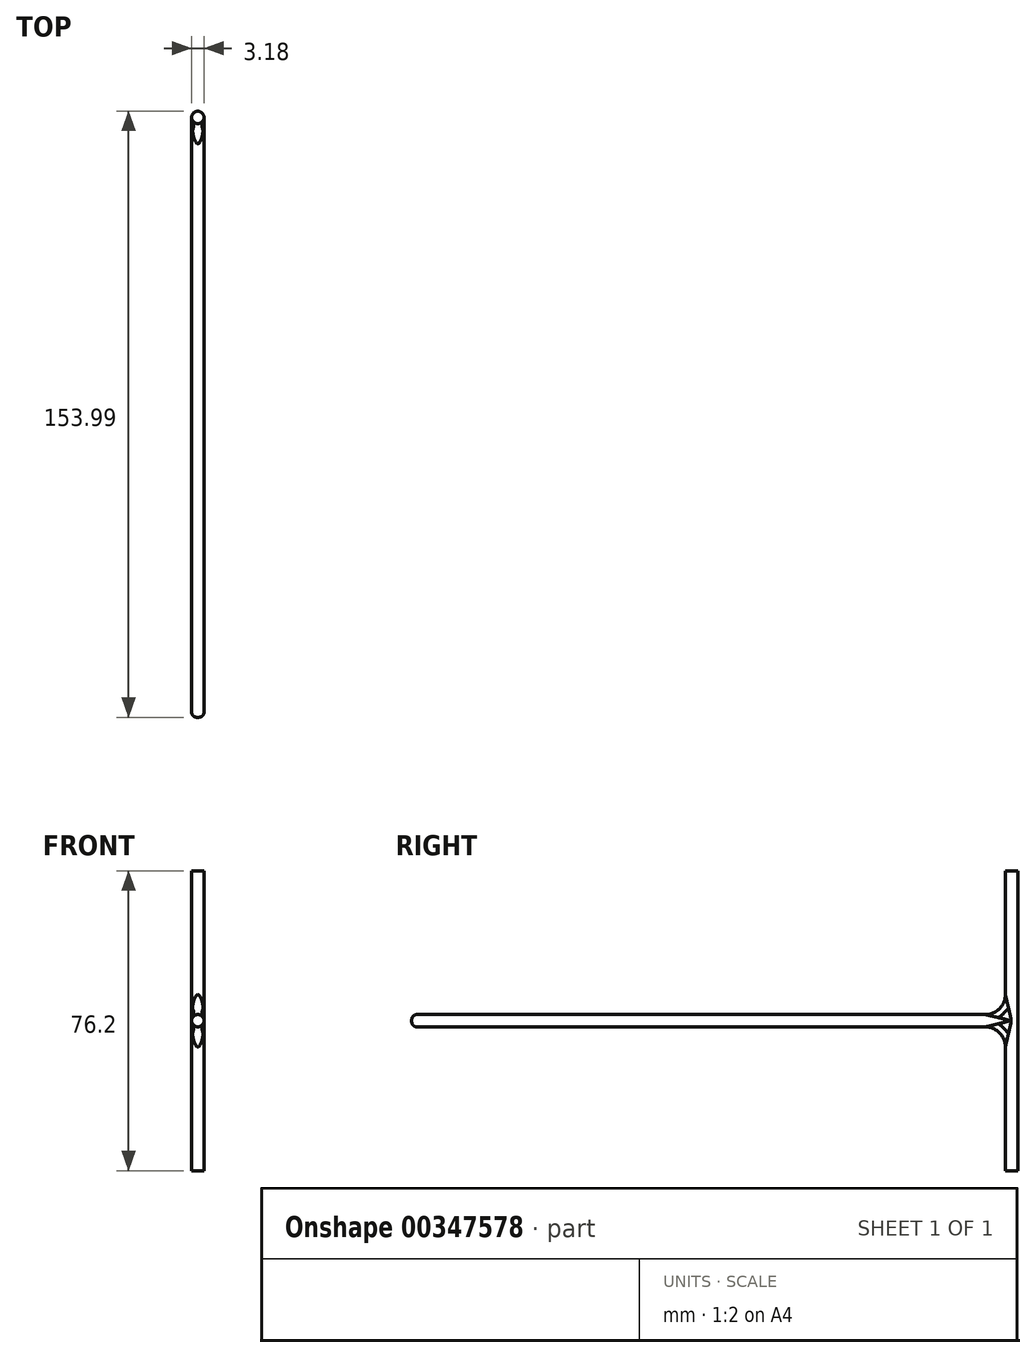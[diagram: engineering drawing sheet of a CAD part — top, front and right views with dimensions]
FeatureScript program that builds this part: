
annotation { "Feature Type Name" : "Feature", "Feature Type Description" : "" }
export const myFeature = defineFeature(function(context is Context, id is Id, definition is map)
    precondition{}
    {
        {
            var Q0;
            Q0=qCreatedBy(makeId("Front.planeOp"),FACE);
            var sketch = newSketch(context, id + "F0", { "sketchPlane" : qUnion([Q0])});
            skCircle(sketch, "E0", {"center": v(0, 0) * mm, "radius": 1.56 * mm});
            skSolve(sketch);
        }
        {
            var Q0;
            Q0 = qSketchRegion(id + "F0", true);
            extrude(context, id + "F1", {"entities" : qUnion([Q0]), "depth" : 152.4 * mm});
        }
        {
            var Q0;
            Q0=makeQuery(id+"F1.opExtrude","CAP_EDGE",EDGE,{"disambiguationData":[OSD([sQuery(id+"F0.wireOp",EDGE,"E0")])],"isStart":false});
            fillet(context, id + "F2", {"entities" : qUnion([Q0]), "radius" : 1.27 * mm, "tangentPropagation" : true, "allowEdgeOverflow" : false});
        }
        {
            var Q0;
            Q0=qCreatedBy(makeId("Top.planeOp"),FACE);
            var sketch = newSketch(context, id + "F3", { "sketchPlane" : qUnion([Q0])});
            skCircle(sketch, "E1", {"center": v(0, 0) * mm, "radius": 1.59 * mm});
            skSolve(sketch);
        }
        {
            var Q0;
            Q0 = qSketchRegion(id + "F3", true);
            extrude(context, id + "F4", {"entities" : qUnion([Q0]), "operationType" : NewBodyOperationType.ADD, "endBound" : BoundingType.SYMMETRIC, "depth" : 76.2 * mm});
        }
        {
            var Q0;
            Q0=makeQuery(id+"F4.boolean.opBoolean","INTERSECT",EDGE,{"derivedFrom":[makeQuery(id+"F1.opExtrude","SWEPT_FACE",FACE,{"disambiguationData":[OSD([sQuery(id+"F0.wireOp",EDGE,"E0")])]}),makeQuery(id+"F4.opExtrude","SWEPT_FACE",FACE,{"disambiguationData":[OSD([sQuery(id+"F3.wireOp",EDGE,"E1")])]})]});
            fillet(context, id + "F5", {"entities" : qUnion([Q0]), "radius" : 5.08 * mm, "tangentPropagation" : true, "allowEdgeOverflow" : false});
        }
    });
